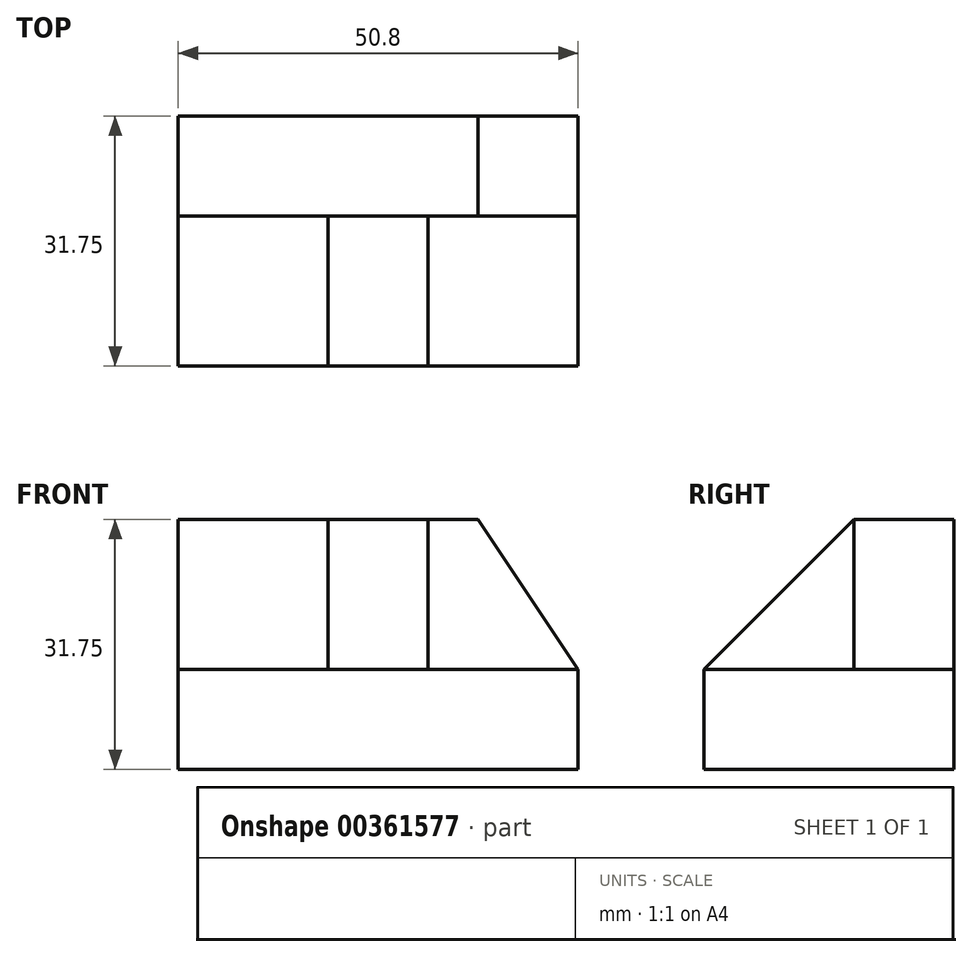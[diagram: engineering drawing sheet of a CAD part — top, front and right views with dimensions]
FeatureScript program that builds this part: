
annotation { "Feature Type Name" : "Feature", "Feature Type Description" : "" }
export const myFeature = defineFeature(function(context is Context, id is Id, definition is map)
    precondition{}
    {
        {
            var Q0;
            Q0=qCreatedBy(makeId("Front.planeOp"),FACE);
            var sketch = newSketch(context, id + "F0", { "sketchPlane" : qUnion([Q0])});
            skLineSegment(sketch, "E0", {"start": v(0, 0) * mm, "end": v(50.8, 0) * mm});
            skLineSegment(sketch, "E1", {"start": v(50.8, 0) * mm, "end": v(50.8, 31.75) * mm});
            skLineSegment(sketch, "E2", {"start": v(50.8, 31.75) * mm, "end": v(0, 31.75) * mm});
            skLineSegment(sketch, "E3", {"start": v(0, 31.75) * mm, "end": v(0, 0) * mm});
            skSolve(sketch);
        }
        {
            var Q0;
            Q0=makeQuery(id+"F0.imprint","IMPRINT",FACE,{"disambiguationData":[TD([[makeQuery(id+"F0.imprint","IMPRINT",EDGE,{"derivedFrom":sQuery(id+"F0.wireOp",EDGE,"E0")}),1.0]])]});
            extrude(context, id + "F1", {"entities" : qUnion([Q0]), "depth" : 31.75 * mm});
        }
        {
            var Q0;
            Q0=makeQuery(id+"F1.opExtrude","CAP_FACE",FACE,{"disambiguationData":[OSD([sQuery(id+"F0.wireOp",EDGE,"E0"),sQuery(id+"F0.wireOp",EDGE,"E1"),sQuery(id+"F0.wireOp",EDGE,"E2"),sQuery(id+"F0.wireOp",EDGE,"E3")])],"isStart":false});
            var sketch = newSketch(context, id + "F2", { "sketchPlane" : qUnion([Q0])});
            skLineSegment(sketch, "E4", {"start": v(31.75, 31.75) * mm, "end": v(31.75, 12.7) * mm});
            skLineSegment(sketch, "E5", {"start": v(31.75, 12.7) * mm, "end": v(50.8, 12.7) * mm});
            skSolve(sketch);
        }
        {
            var Q0;
            {var subQ0=sQuery(id+"F2.wireOp",EDGE,"E4");Q0=makeQuery(id+"F2.imprint","IMPRINT",FACE,{"disambiguationData":[TD([[makeQuery(id+"F2.imprint","IMPRINT",EDGE,{"derivedFrom":subQ0}),1.0]])]});}
            extrude(context, id + "F3", {"entities" : qUnion([Q0]), "operationType" : NewBodyOperationType.REMOVE, "oppositeDirection" : true, "depth" : 19.05 * mm});
        }
        {
            var Q0;
            Q0=makeQuery(id+"F1.opExtrude","CAP_FACE",FACE,{"disambiguationData":[OSD([sQuery(id+"F0.wireOp",EDGE,"E0"),sQuery(id+"F0.wireOp",EDGE,"E1"),sQuery(id+"F0.wireOp",EDGE,"E2"),sQuery(id+"F0.wireOp",EDGE,"E3")])],"isStart":true});
            var sketch = newSketch(context, id + "F4", { "sketchPlane" : qUnion([Q0])});
            skLineSegment(sketch, "E6", {"start": v(-38.1, 31.75) * mm, "end": v(-50.8, 12.7) * mm});
            skSolve(sketch);
        }
        {
            var Q0;
            {var subQ0=sQuery(id+"F4.wireOp",EDGE,"E6");Q0=makeQuery(id+"F4.imprint","IMPRINT",FACE,{"disambiguationData":[TD([[makeQuery(id+"F4.imprint","IMPRINT",EDGE,{"derivedFrom":subQ0}),-1.0]])]});}
            extrude(context, id + "F5", {"entities" : qUnion([Q0]), "operationType" : NewBodyOperationType.REMOVE, "oppositeDirection" : true, "depth" : 12.7 * mm});
        }
        {
            var Q0;
            Q0=makeQuery(id+"F1.opExtrude","SWEPT_FACE",FACE,{"disambiguationData":[OSD([sQuery(id+"F0.wireOp",EDGE,"E3")])]});
            var sketch = newSketch(context, id + "F6", { "sketchPlane" : qUnion([Q0])});
            skLineSegment(sketch, "E7", {"start": v(12.7, 31.75) * mm, "end": v(31.75, 12.7) * mm});
            skSolve(sketch);
        }
        {
            var Q0;
            {var subQ0=sQuery(id+"F6.wireOp",EDGE,"E7");Q0=makeQuery(id+"F6.imprint","IMPRINT",FACE,{"disambiguationData":[TD([[makeQuery(id+"F6.imprint","IMPRINT",EDGE,{"derivedFrom":subQ0}),1.0]])]});}
            extrude(context, id + "F7", {"entities" : qUnion([Q0]), "operationType" : NewBodyOperationType.REMOVE, "oppositeDirection" : true, "depth" : 31.75 * mm});
        }
        {
            var Q0;
            Q0=makeQuery(id+"F1.opExtrude","SWEPT_FACE",FACE,{"disambiguationData":[OSD([sQuery(id+"F0.wireOp",EDGE,"E3")])]});
            var sketch = newSketch(context, id + "F8", { "sketchPlane" : qUnion([Q0])});
            skLineSegment(sketch, "E8", {"start": v(12.7, 31.75) * mm, "end": v(12.7, 12.7) * mm});
            skLineSegment(sketch, "E9", {"start": v(12.7, 12.7) * mm, "end": v(31.75, 12.7) * mm});
            skSolve(sketch);
        }
        {
            var Q0;
            Q0=makeQuery(id+"F8.imprint","IMPRINT",FACE,{"disambiguationData":[TD([[makeQuery(id+"F8.imprint","IMPRINT",EDGE,{"derivedFrom":sQuery(id+"F8.wireOp",EDGE,"E8")}),1.0]])]});
            extrude(context, id + "F9", {"entities" : qUnion([Q0]), "operationType" : NewBodyOperationType.REMOVE, "oppositeDirection" : true, "depth" : 19.05 * mm});
        }
    });
